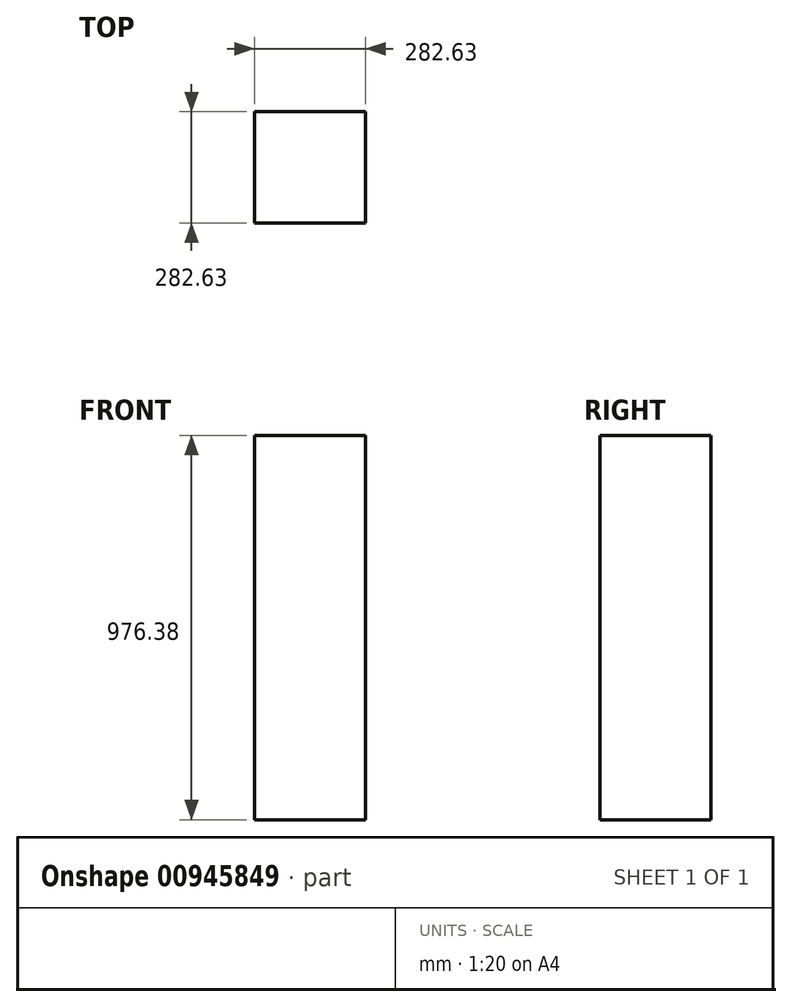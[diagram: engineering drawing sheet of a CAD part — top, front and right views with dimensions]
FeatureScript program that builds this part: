
annotation { "Feature Type Name" : "Feature", "Feature Type Description" : "" }
export const myFeature = defineFeature(function(context is Context, id is Id, definition is map)
    precondition{}
    {
        {
            var Q0;
            Q0=qCreatedBy(makeId("Top.planeOp"),FACE);
            var sketch = newSketch(context, id + "F0", { "sketchPlane" : qUnion([Q0])});
            skLineSegment(sketch, "E0.bottom", {"start": v(-282.63, 282.63) * mm, "end": v(0, 282.63) * mm});
            skLineSegment(sketch, "E0.top", {"start": v(-282.63, 0) * mm, "end": v(0, 0) * mm});
            skLineSegment(sketch, "E0.left", {"start": v(-282.63, 282.63) * mm, "end": v(-282.63, 0) * mm});
            skLineSegment(sketch, "E0.right", {"start": v(0, 282.63) * mm, "end": v(0, 0) * mm});
            skSolve(sketch);
        }
        {
            var Q0;
            Q0=makeQuery(id+"F0.imprint","IMPRINT",FACE,{"disambiguationData":[TD([[makeQuery(id+"F0.imprint","IMPRINT",EDGE,{"derivedFrom":sQuery(id+"F0.wireOp",EDGE,"E0.bottom")}),-1.0]])]});
            extrude(context, id + "F1", {"entities" : qUnion([Q0]), "depth" : 976.38 * mm, "offsetDistance" : 25.4 * mm});
        }
    });
